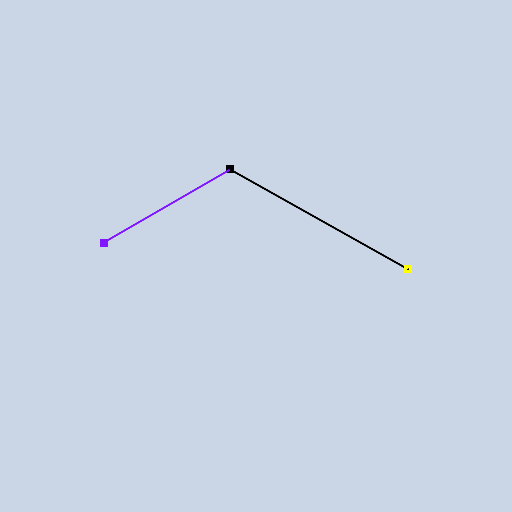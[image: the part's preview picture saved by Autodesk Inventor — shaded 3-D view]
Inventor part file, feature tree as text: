
AUTODESK INVENTOR PART (.ipt)
format: ipt  version: 2025 (Build 290162000, 162)  size: 153,600 bytes
history: native  units: in
note: dims shown in document units (in); Inventor stores cm internally (conversion verified against a paired STEP export)
features: other x2, plane x1, sketch x1
ambient origin geometry x8: Origin, YZ Plane, XZ Plane, XY Plane, X Axis, Y Axis, Z Axis, Center Point
feature tree (4):
  other  "Work Point1"
  other  "Work Point2"
  plane  "Work Plane1"
  sketch  "3D Sketch1"
